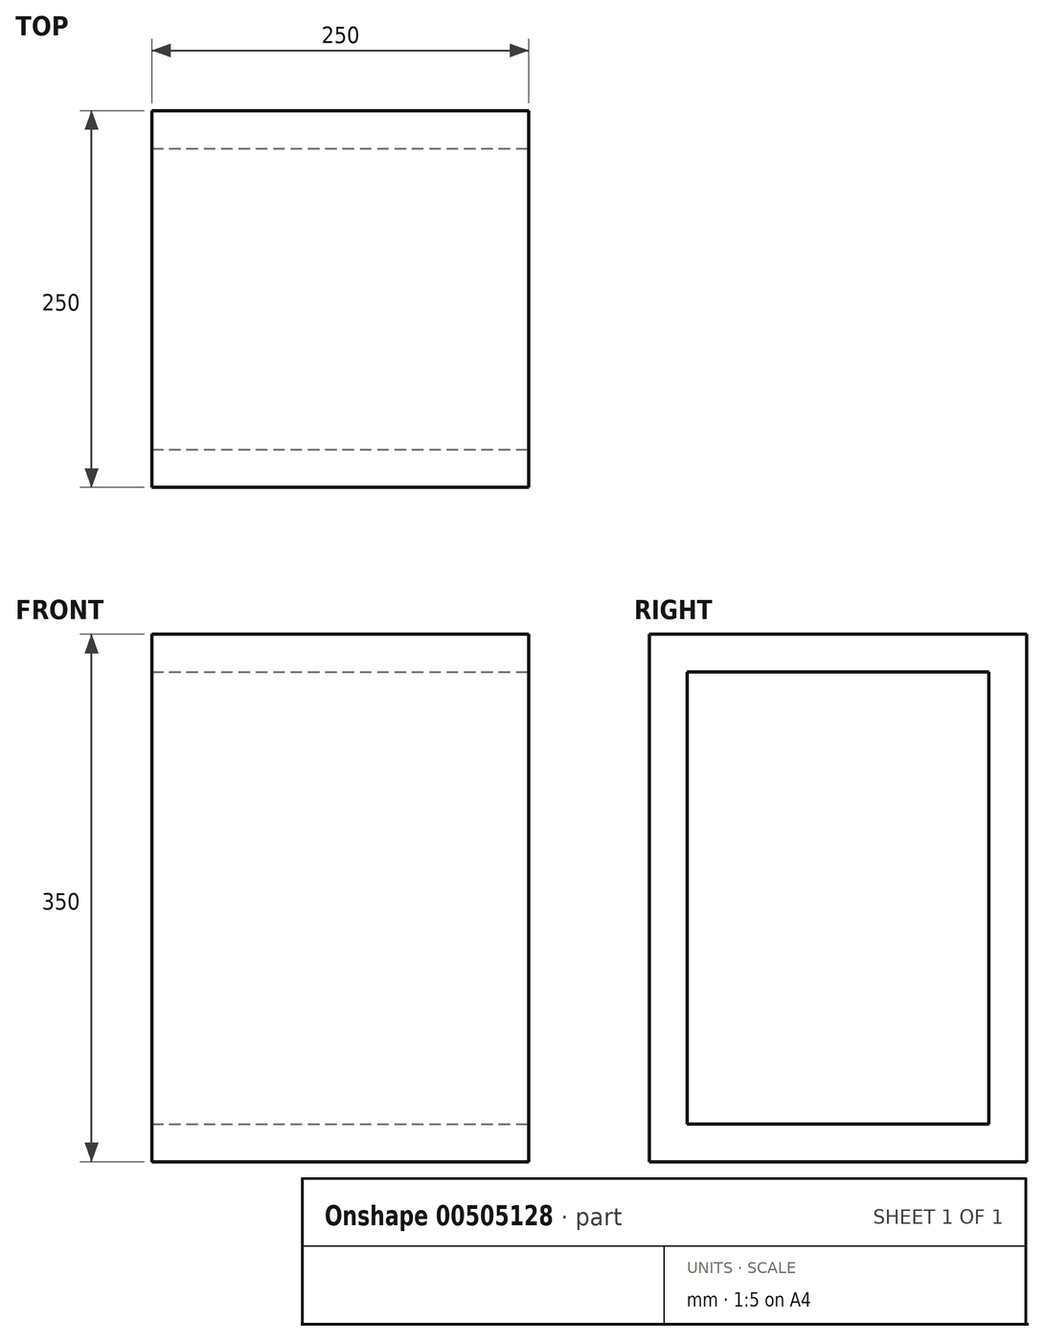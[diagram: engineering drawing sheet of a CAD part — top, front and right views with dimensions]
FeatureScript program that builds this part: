
annotation { "Feature Type Name" : "Feature", "Feature Type Description" : "" }
export const myFeature = defineFeature(function(context is Context, id is Id, definition is map)
    precondition{}
    {
        {
            var Q0;
            Q0=qCreatedBy(makeId("Front.planeOp"),FACE);
            var sketch = newSketch(context, id + "F0", { "sketchPlane" : qUnion([Q0])});
            skLineSegment(sketch, "E0.bottom", {"start": v(0, 0) * mm, "end": v(-250, 0) * mm});
            skLineSegment(sketch, "E0.top", {"start": v(0, 350) * mm, "end": v(-250, 350) * mm});
            skLineSegment(sketch, "E0.left", {"start": v(0, 0) * mm, "end": v(0, 350) * mm});
            skLineSegment(sketch, "E0.right", {"start": v(-250, 0) * mm, "end": v(-250, 350) * mm});
            skSolve(sketch);
        }
        {
            var Q0;
            Q0=qSketchRegion(id+"F0",true);
            extrude(context, id + "F1", {"entities" : qUnion([Q0]), "depth" : 250 * mm});
        }
        {
            var Q0;
            Q0=makeQuery(id+"F1.opExtrude","SWEPT_FACE",FACE,{"disambiguationData":[OSD([sQuery(id+"F0.wireOp",EDGE,"E0.left")])]});
            var sketch = newSketch(context, id + "F2", { "sketchPlane" : qUnion([Q0])});
            skLineSegment(sketch, "E1.0", {"start": v(-225, 325) * mm, "end": v(-25, 325) * mm});
            skLineSegment(sketch, "E1.1", {"start": v(-225, 25) * mm, "end": v(-225, 325) * mm});
            skLineSegment(sketch, "E1.2", {"start": v(-225, 25) * mm, "end": v(-25, 25) * mm});
            skLineSegment(sketch, "E1.3", {"start": v(-25, 25) * mm, "end": v(-25, 325) * mm});
            skSolve(sketch);
        }
        {
            var Q0;
            Q0=qSketchRegion(id+"F2",true);
            extrude(context, id + "F3", {"entities" : qUnion([Q0]), "operationType" : NewBodyOperationType.REMOVE, "endBound" : BoundingType.THROUGH_ALL, "oppositeDirection" : true, "depth" : 25 * mm});
        }
    });
